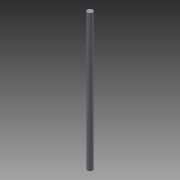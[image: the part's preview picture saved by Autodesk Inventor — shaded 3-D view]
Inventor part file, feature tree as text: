
AUTODESK INVENTOR PART (.ipt)
format: ipt  version: 2015 SP1 (Build 190203100, 203)  size: 62,976 bytes
history: native  units: mm
features: other x3, sketch x1
ambient origin geometry x8: Origin, YZ Plane, XZ Plane, XY Plane, X Axis, Y Axis, Z Axis, Center Point
bodies: Solid1 (feature_tree)
feature tree (4):
  other  "tige.ipt"
  other  "Solid1::tige.ipt"
  other  "TaggingFeature1"
  sketch  "Sketch1"  dims[d0=10.0mm]
